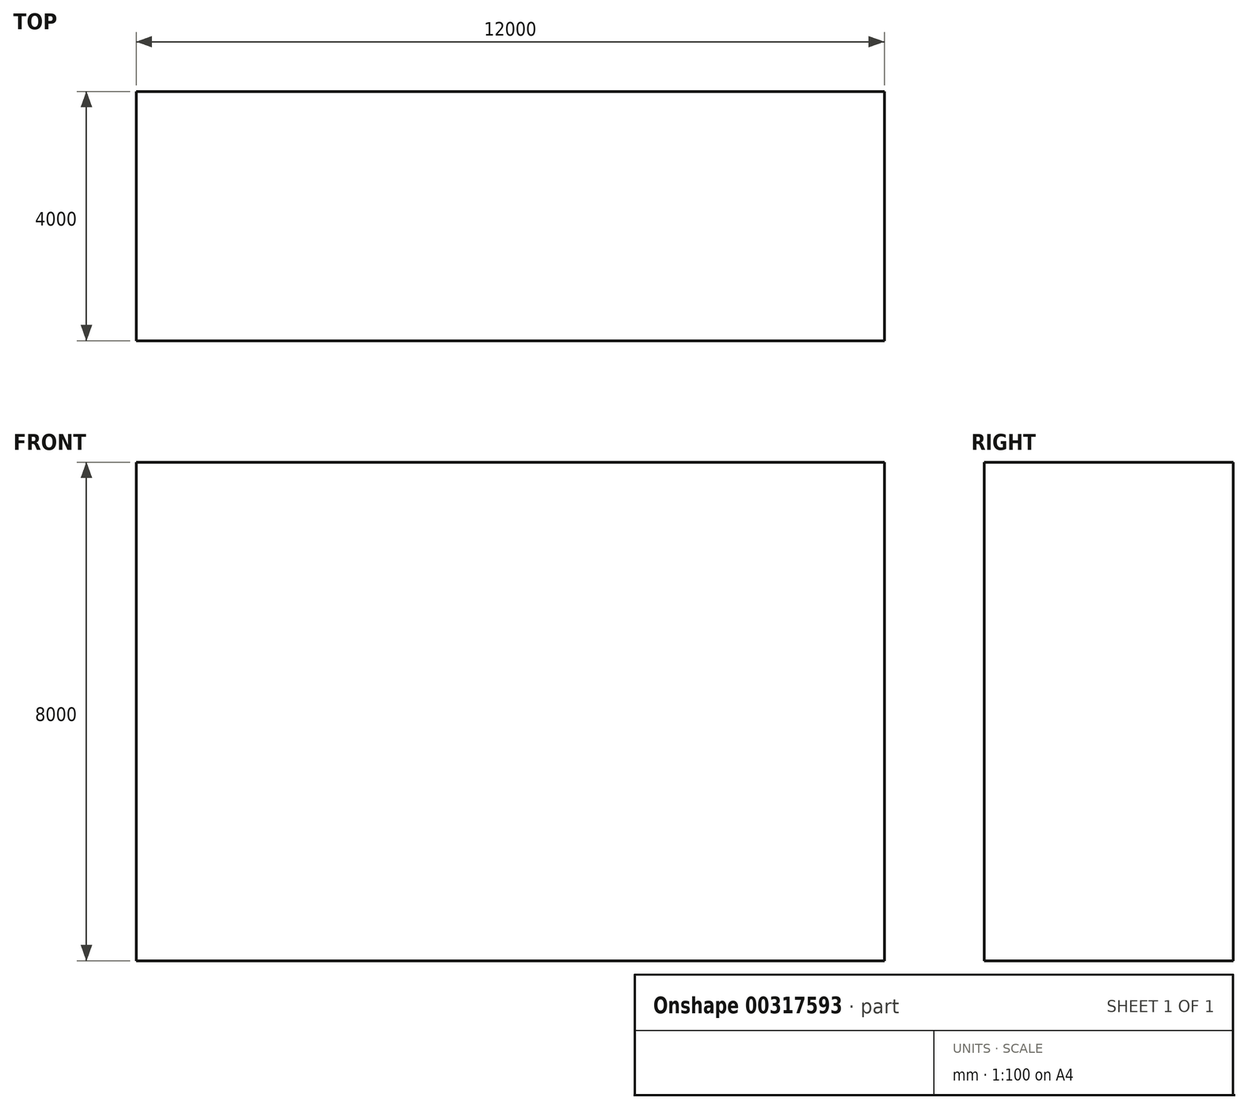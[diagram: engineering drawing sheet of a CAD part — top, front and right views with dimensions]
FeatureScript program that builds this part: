
annotation { "Feature Type Name" : "Feature", "Feature Type Description" : "" }
export const myFeature = defineFeature(function(context is Context, id is Id, definition is map)
    precondition{}
    {
        {
            var Q0;
            Q0=qCreatedBy(makeId("Front.planeOp"),FACE);
            var sketch = newSketch(context, id + "F0", { "sketchPlane" : qUnion([Q0])});
            skLineSegment(sketch, "E0.bottom", {"start": v(-5994.62, 5023.21) * mm, "end": v(6005.38, 5023.21) * mm});
            skLineSegment(sketch, "E0.top", {"start": v(-5994.62, -2976.79) * mm, "end": v(6005.38, -2976.79) * mm});
            skLineSegment(sketch, "E0.left", {"start": v(-5994.62, 5023.21) * mm, "end": v(-5994.62, -2976.79) * mm});
            skLineSegment(sketch, "E0.right", {"start": v(6005.38, 5023.21) * mm, "end": v(6005.38, -2976.79) * mm});
            skLineSegment(sketch, "E1", {"start": v(0, 5023.21) * mm, "end": v(0, -2976.79) * mm});
            skSolve(sketch);
        }
        {
            var Q0;
            Q0 = qSketchRegion(id + "F0", true);
            extrude(context, id + "F1", {"entities" : qUnion([Q0]), "depth" : 4000 * mm});
        }
    });
